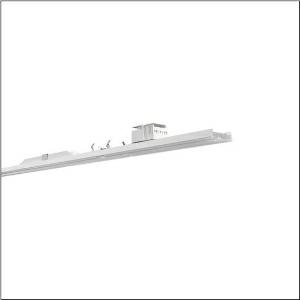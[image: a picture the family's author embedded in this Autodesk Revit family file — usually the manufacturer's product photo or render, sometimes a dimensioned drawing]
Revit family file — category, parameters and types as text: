
# Revit family: licross_r__21_recessed_mo_52tl18dne75f_0d69
name_source: partatom
category: Lighting Fixtures
units: mm (PartAtom-declared; Revit-internal decimal feet)

## family parameters
Cut with Voids When Loaded = No
Host = Face
Light Source = No
Part Type = Normal
Room Calculation Point = No
Round Connector Dimension = Use Diameter
Shared = No

## types (1)
- --- (1 x LED, 7740 lm, 61.1 W, 5000K)
    Apparent Load = 61 VA
    CIE Flux Codes = 79 95 99 100 100
    Color Rendering = 90
    Color Temperature = 5000K
    Default Elevation = 1800 mm
    Description = Licross® 21 Recessed MO, luminaire insert, of sheet steel, galvanised, coil coated, white, length: 1.500mm, width: 66mm, height: 67mm, LED rated luminous flux: 7.740lm, light colour: 950, control gear: DALI 2, control gear: ECG DALI, with plug, 5-pole, with phase selection, mains connection: 220..240V, AC, 50/60Hz, halogen-free wiring, primary optical cover: cover, of PMMA, light emission: direct distribution, protection rating (complete): IP40, insulation class (complete): insulation class I (protective earthing), certification: CE, ENEC, VDE, UKCA, protection symbol: D if used in an environment without relevant dust loads with corresponding accessories, permissible ambient temperature for indoor applications: -25..+35°C, corresponds to IFS (International Featured Standards) requirements for safety and quality in the food industry, reducing of maximum allowable ambient temperature of 5°C with ceiling mounting, packaging unit: 1 piece
    Height = 58 mm
    Lamp = 1 x LED
    Lamp Light Flux = 7740 lm
    Lamp Power = 61.1 W
    Lamp count = 1
    Length = 1500 mm
    Luminous efficacy = 127 lm/W
    Manufacturer = Siteco
    ModVariant = No
    Model = 52TL18DNE75F
    Mounting Place = Ceiling
    Mounting Type = Pendant
    Number of Poles = 1
    OnlyDefault = Yes
    Power Factor = 1
    Product Name = Licross® 21 Recessed MO
    Product group = luminaire insert
    ProductGroupID = 902
    Protection Class = Protection class I
    Protection Degree = IP 40
    RLX_Detail_Level = 1
    RlxData = <blob elided: 22405 chars, md5=38ad9bd6>
    Socket = socket
    Standby Power = 0 W
    System Light Flux = 7740 lm
    System Power = 61 W
    Type Comments = factory setting: luminous flux: 100 % | dim-lin: 254 | 405 mA
    Type Image = l_1266722.jpg
    URL = http://relux.com
    VarID = @adj_128777
    Voltage = 0 V
    Weight = 0.00 kg
    Width = 66 mm

## geometry (parser evidence)
native form markers: Blend x4, Sweep x9
no freeform markers — native parametric forms only
